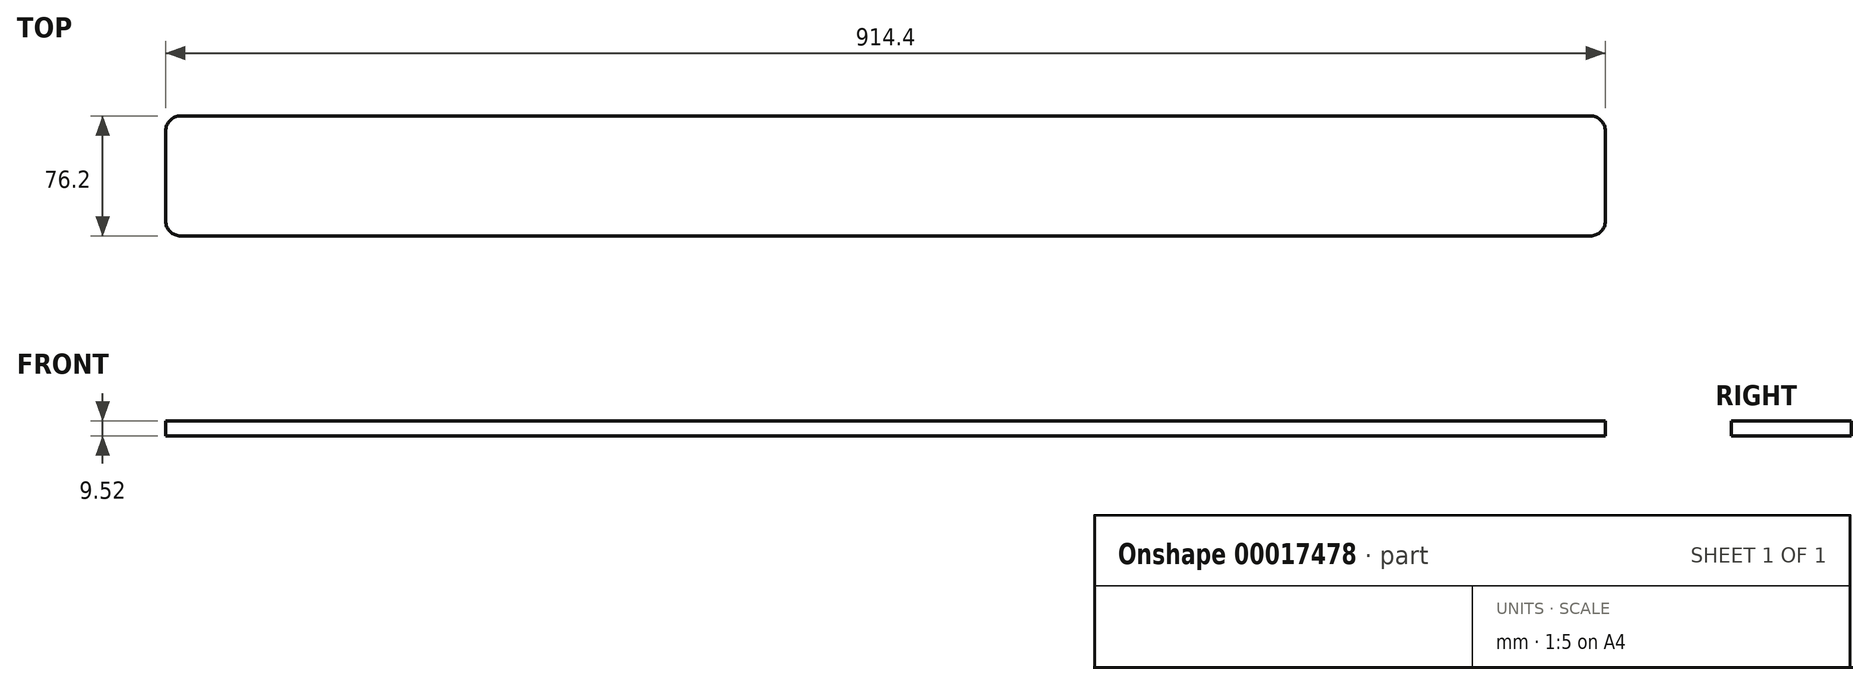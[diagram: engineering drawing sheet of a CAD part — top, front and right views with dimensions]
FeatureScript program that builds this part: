
annotation { "Feature Type Name" : "Feature", "Feature Type Description" : "" }
export const myFeature = defineFeature(function(context is Context, id is Id, definition is map)
    precondition{}
    {
        {
            var Q0;
            Q0=qCreatedBy(makeId("Top.planeOp"),FACE);
            var sketch = newSketch(context, id + "F0", { "sketchPlane" : qUnion([Q0])});
            skLineSegment(sketch, "E0.rect.bottom", {"start": v(457.2, 38.1) * mm, "end": v(-457.2, 38.1) * mm});
            skLineSegment(sketch, "E0.rect.top", {"start": v(457.2, -38.1) * mm, "end": v(-457.2, -38.1) * mm});
            skLineSegment(sketch, "E0.rect.left", {"start": v(457.2, 38.1) * mm, "end": v(457.2, -38.1) * mm});
            skLineSegment(sketch, "E0.rect.right", {"start": v(-457.2, 38.1) * mm, "end": v(-457.2, -38.1) * mm});
            skPoint(sketch, "E0.rect.middle", {"position": v(0, 0) * mm});
            skSolve(sketch);
        }
        {
            var Q0;
            Q0 = qSketchRegion(id + "F0", true);
            extrude(context, id + "F1", {"entities" : qUnion([Q0]), "endBound" : BoundingType.SYMMETRIC, "depth" : 9.52 * mm});
        }
        {
            var Q0;
            Q0=makeQuery(id+"F1.opExtrude","SWEPT_EDGE",EDGE,{"disambiguationData":[OSD([sQuery(id+"F0.wireOp",EDGE,"E0.rect.top"),sQuery(id+"F0.wireOp",EDGE,"E0.rect.right")])]});
            var Q1;
            Q1=makeQuery(id+"F1.opExtrude","SWEPT_EDGE",EDGE,{"disambiguationData":[OSD([sQuery(id+"F0.wireOp",EDGE,"E0.rect.bottom"),sQuery(id+"F0.wireOp",EDGE,"E0.rect.right")])]});
            var Q2;
            Q2=makeQuery(id+"F1.opExtrude","SWEPT_EDGE",EDGE,{"disambiguationData":[OSD([sQuery(id+"F0.wireOp",EDGE,"E0.rect.top"),sQuery(id+"F0.wireOp",EDGE,"E0.rect.left")])]});
            var Q3;
            Q3=makeQuery(id+"F1.opExtrude","SWEPT_EDGE",EDGE,{"disambiguationData":[OSD([sQuery(id+"F0.wireOp",EDGE,"E0.rect.bottom"),sQuery(id+"F0.wireOp",EDGE,"E0.rect.left")])]});
            fillet(context, id + "F2", {"entities" : qUnion([Q0, Q1, Q2, Q3]), "radius" : 9.52 * mm, "tangentPropagation" : true, "allowEdgeOverflow" : false});
        }
    });
